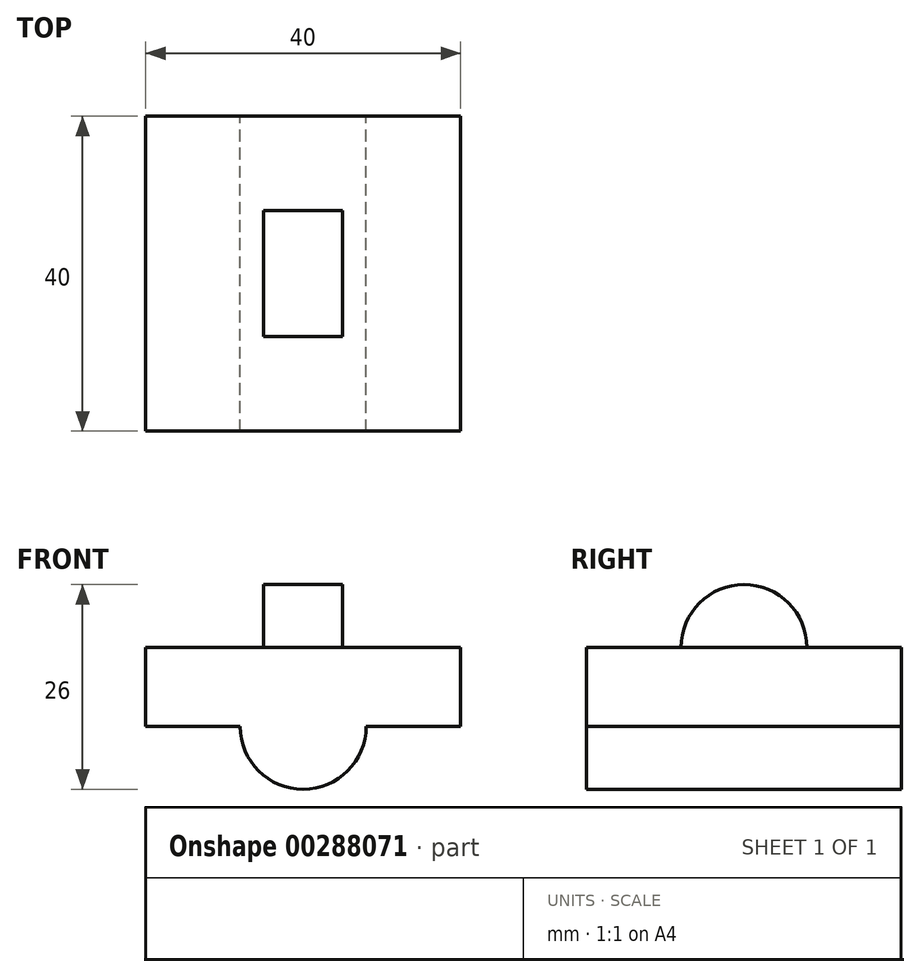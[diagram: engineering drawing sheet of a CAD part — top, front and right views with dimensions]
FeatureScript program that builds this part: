
annotation { "Feature Type Name" : "Feature", "Feature Type Description" : "" }
export const myFeature = defineFeature(function(context is Context, id is Id, definition is map)
    precondition{}
    {
        {
            var Q0;
            Q0=qCreatedBy(makeId("Front.planeOp"),FACE);
            var sketch = newSketch(context, id + "F0", { "sketchPlane" : qUnion([Q0])});
            skCircle(sketch, "E0", {"center": v(0, 0) * mm, "radius": 8 * mm});
            skLineSegment(sketch, "E1.bottom", {"start": v(20, 0) * mm, "end": v(-20, 0) * mm});
            skLineSegment(sketch, "E1.top", {"start": v(20, 10) * mm, "end": v(-20, 10) * mm});
            skLineSegment(sketch, "E1.left", {"start": v(20, 0) * mm, "end": v(20, 10) * mm});
            skLineSegment(sketch, "E1.right", {"start": v(-20, 0) * mm, "end": v(-20, 10) * mm});
            skPoint(sketch, "E1.middle", {"position": v(0, 5) * mm});
            skSolve(sketch);
        }
        {
            var Q0;
            Q0 = qSketchRegion(id + "F0", true);
            extrude(context, id + "F1", {"entities" : qUnion([Q0]), "endBound" : BoundingType.SYMMETRIC, "depth" : 40 * mm});
        }
        {
            var Q0;
            Q0=qCreatedBy(makeId("Right.planeOp"),FACE);
            var sketch = newSketch(context, id + "F2", { "sketchPlane" : qUnion([Q0])});
            skCircle(sketch, "E2", {"center": v(0, 10) * mm, "radius": 8 * mm});
            skSolve(sketch);
        }
        {
            var Q0;
            Q0=makeQuery(id+"F2.imprint","IMPRINT",FACE,{"disambiguationData":[TD([[makeQuery(id+"F2.imprint","IMPRINT",EDGE,{"derivedFrom":sQuery(id+"F2.wireOp",EDGE,"E2")}),1.0]])]});
            extrude(context, id + "F3", {"entities" : qUnion([Q0]), "operationType" : NewBodyOperationType.ADD, "endBound" : BoundingType.SYMMETRIC, "depth" : 10 * mm});
        }
    });
